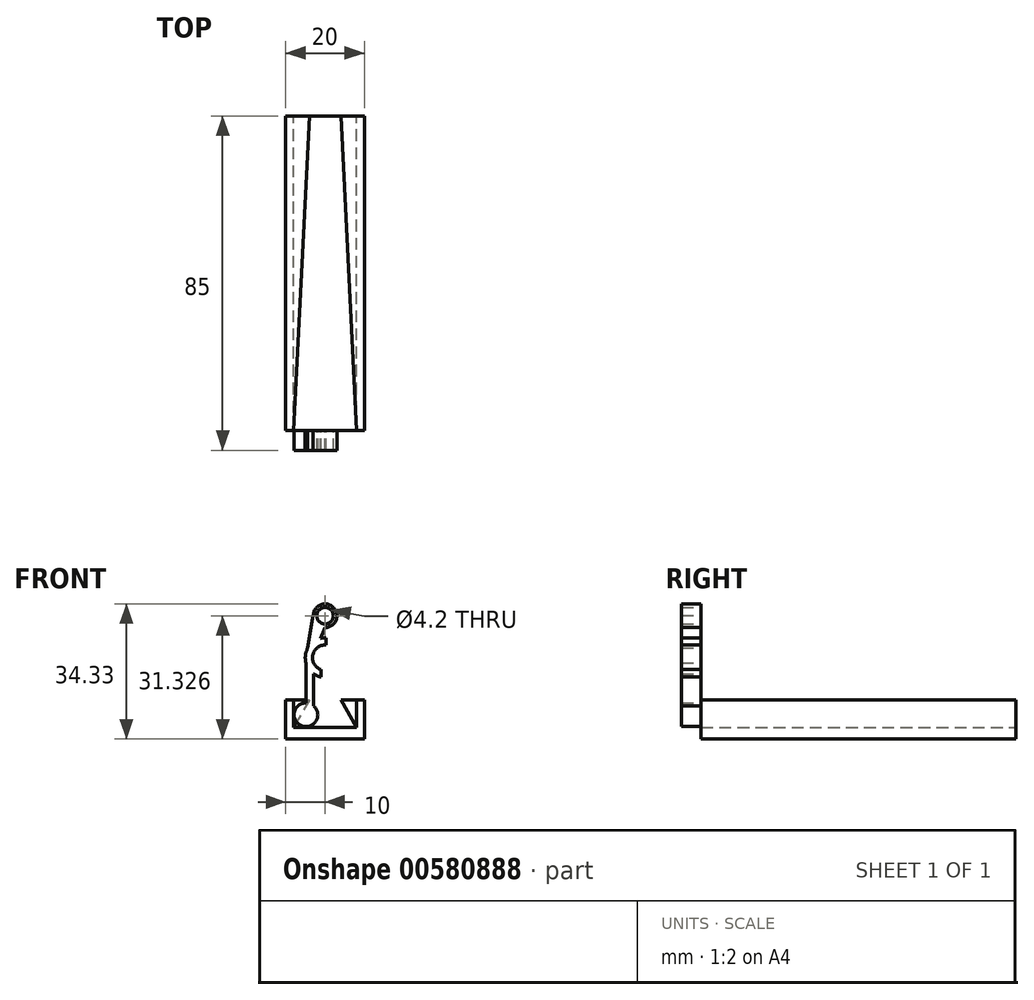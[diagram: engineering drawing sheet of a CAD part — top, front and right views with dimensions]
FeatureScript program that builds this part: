
annotation { "Feature Type Name" : "Feature", "Feature Type Description" : "" }
export const myFeature = defineFeature(function(context is Context, id is Id, definition is map)
    precondition{}
    {
        {
            var Q0;
            Q0=qCreatedBy(makeId("Front.planeOp"),FACE);
            var sketch = newSketch(context, id + "F0", { "sketchPlane" : qUnion([Q0])});
            skLineSegment(sketch, "E0.bottom", {"start": v(-10, 0) * mm, "end": v(10, 0) * mm});
            skLineSegment(sketch, "E0.top", {"start": v(-10, 10) * mm, "end": v(10, 10) * mm});
            skLineSegment(sketch, "E0.left", {"start": v(-10, 0) * mm, "end": v(-10, 10) * mm});
            skLineSegment(sketch, "E0.right", {"start": v(10, 0) * mm, "end": v(10, 10) * mm});
            skSolve(sketch);
        }
        {
            var Q0;
            Q0=makeQuery(id+"F0.imprint","IMPRINT",FACE,{"disambiguationData":[TD([[makeQuery(id+"F0.imprint","IMPRINT",EDGE,{"derivedFrom":sQuery(id+"F0.wireOp",EDGE,"E0.bottom")}),1.0]])]});
            extrude(context, id + "F1", {"entities" : qUnion([Q0]), "oppositeDirection" : true, "depth" : 80 * mm, "offsetDistance" : 25 * mm});
        }
        {
            var Q0;
            Q0=makeQuery(id+"F1.opExtrude","CAP_FACE",FACE,{"disambiguationData":[OSD([sQuery(id+"F0.wireOp",EDGE,"E0.bottom"),sQuery(id+"F0.wireOp",EDGE,"E0.top"),sQuery(id+"F0.wireOp",EDGE,"E0.left"),sQuery(id+"F0.wireOp",EDGE,"E0.right")])],"isStart":true});
            var sketch = newSketch(context, id + "F2", { "sketchPlane" : qUnion([Q0])});
            skLineSegment(sketch, "E1", {"start": v(0, 0) * mm, "end": v(0, 12.76) * mm, "construction": true});
            skLineSegment(sketch, "E2", {"start": v(-8, 10) * mm, "end": v(8, 10) * mm});
            skLineSegment(sketch, "E3", {"start": v(-8, 10) * mm, "end": v(-8, 3) * mm});
            skLineSegment(sketch, "E4", {"start": v(-8, 3) * mm, "end": v(8, 3) * mm});
            skLineSegment(sketch, "E5", {"start": v(8, 10) * mm, "end": v(8, 3) * mm});
            skSolve(sketch);
        }
        {
            var Q0;
            Q0=makeQuery(id+"F1.opExtrude","CAP_FACE",FACE,{"disambiguationData":[OSD([sQuery(id+"F0.wireOp",EDGE,"E0.bottom"),sQuery(id+"F0.wireOp",EDGE,"E0.top"),sQuery(id+"F0.wireOp",EDGE,"E0.left"),sQuery(id+"F0.wireOp",EDGE,"E0.right")])],"isStart":false});
            var sketch = newSketch(context, id + "F3", { "sketchPlane" : qUnion([Q0])});
            skLineSegment(sketch, "E6", {"start": v(-4, 10) * mm, "end": v(4, 10) * mm});
            skLineSegment(sketch, "E7", {"start": v(4, 10) * mm, "end": v(8, 3) * mm});
            skLineSegment(sketch, "E8", {"start": v(8, 3) * mm, "end": v(-8, 3) * mm});
            skLineSegment(sketch, "E9", {"start": v(-8, 3) * mm, "end": v(-4, 10) * mm});
            skSolve(sketch);
        }
        {
            var Q1;
            Q1 = qSketchRegion(id + "F2", true);
            var Q2;
            Q2 = qSketchRegion(id + "F3", true);
            loft(context, id + "F4", {"operationType" : NewBodyOperationType.REMOVE, "sheetProfilesArray" : [{ "sheetProfileEntities" : qUnion([Q1]) }, { "sheetProfileEntities" : qUnion([Q2]) }]});
        }
        {
            var Q0;
            Q0=qCreatedBy(makeId("Front.planeOp"),FACE);
            var sketch = newSketch(context, id + "F5", { "sketchPlane" : qUnion([Q0])});
            skLineSegment(sketch, "E10", {"start": v(0, 0) * mm, "end": v(0, 38.74) * mm, "construction": true});
            skCircle(sketch, "E11", {"center": v(0, 31.33) * mm, "radius": 3 * mm});
            skCircle(sketch, "E12", {"center": v(-4.85, 6.17) * mm, "radius": 3.01 * mm});
            skLineSegment(sketch, "E13.bottom", {"start": v(-2.9, 19.35) * mm, "end": v(-4.85, 19.35) * mm});
            skLineSegment(sketch, "E13.top", {"start": v(-2.9, 6.17) * mm, "end": v(-4.85, 6.17) * mm});
            skLineSegment(sketch, "E13.left", {"start": v(-2.9, 19.35) * mm, "end": v(-2.9, 6.17) * mm});
            skLineSegment(sketch, "E13.right", {"start": v(-4.85, 19.35) * mm, "end": v(-4.85, 6.17) * mm});
            skCircle(sketch, "E14", {"center": v(0, 20.68) * mm, "radius": 3.2 * mm});
            skCircle(sketch, "E15", {"center": v(0, 20.68) * mm, "radius": 5.03 * mm});
            skLineSegment(sketch, "E16.bottom", {"start": v(-0.97, 17.63) * mm, "end": v(0.97, 17.63) * mm});
            skLineSegment(sketch, "E16.top", {"start": v(-0.97, 15.08) * mm, "end": v(0.97, 15.08) * mm});
            skLineSegment(sketch, "E16.left", {"start": v(-0.97, 17.63) * mm, "end": v(-0.97, 15.08) * mm});
            skLineSegment(sketch, "E16.right", {"start": v(0.97, 17.63) * mm, "end": v(0.97, 15.08) * mm});
            skLineSegment(sketch, "E17", {"start": v(-3, 31.39) * mm, "end": v(-4.42, 23.08) * mm});
            skLineSegment(sketch, "E18", {"start": v(0, 28.33) * mm, "end": v(-1.17, 25.57) * mm});
            skCircle(sketch, "E19", {"center": v(0, 31.33) * mm, "radius": 2.1 * mm});
            skLineSegment(sketch, "E20", {"start": v(0.19, 25.7) * mm, "end": v(0.19, 23.87) * mm});
            skSolve(sketch);
        }
        {
            var Q0;
            {var subQ5=sQuery(id+"F5.wireOp",EDGE,"E13.top");Q0=makeQuery(id+"F5.imprint","IMPRINT",FACE,{"disambiguationData":[TD([[makeQuery(id+"F5.imprint","IMPRINT",EDGE,{"derivedFrom":subQ5}),1.0]])]});}
            var Q1;
            {var subQ5=sQuery(id+"F5.wireOp",EDGE,"E13.top");Q1=makeQuery(id+"F5.imprint","IMPRINT",FACE,{"disambiguationData":[TD([[makeQuery(id+"F5.imprint","IMPRINT",EDGE,{"derivedFrom":subQ5}),-1.0]])]});}
            var Q2;
            {var subQ0=sQuery(id+"F5.wireOp",EDGE,"E13.left");var subQ1=sQuery(id+"F5.wireOp",EDGE,"E12");var subQ2=makeQuery(id+"F5.imprint","INTERSECT",VERTEX,{"derivedFrom":[subQ1,subQ0]});Q2=makeQuery(id+"F5.imprint","IMPRINT",FACE,{"disambiguationData":[TD([[makeQuery(id+"F5.imprint","IMPRINT",EDGE,{"disambiguationData":[TD([[subQ2,-1.0]])],"derivedFrom":subQ1}),-1.0]])]});}
            var Q3;
            {var subQ1=sQuery(id+"F5.wireOp",EDGE,"E13.left");var subQ3=sQuery(id+"F5.wireOp",EDGE,"E15");var subQ4=makeQuery(id+"F5.imprint","INTERSECT",VERTEX,{"derivedFrom":[subQ1,subQ3]});Q3=makeQuery(id+"F5.imprint","IMPRINT",FACE,{"disambiguationData":[TD([[makeQuery(id+"F5.imprint","IMPRINT",EDGE,{"disambiguationData":[TD([[subQ4,-1.0]])],"derivedFrom":subQ3}),1.0]])]});}
            var Q4;
            {var subQ0=sQuery(id+"F5.wireOp",EDGE,"E13.bottom");Q4=makeQuery(id+"F5.imprint","IMPRINT",FACE,{"disambiguationData":[TD([[makeQuery(id+"F5.imprint","IMPRINT",EDGE,{"derivedFrom":subQ0}),1.0]])]});}
            var Q5;
            {var subQ1=sQuery(id+"F5.wireOp",EDGE,"E13.bottom");Q5=makeQuery(id+"F5.imprint","IMPRINT",FACE,{"disambiguationData":[TD([[makeQuery(id+"F5.imprint","IMPRINT",EDGE,{"derivedFrom":subQ1}),-1.0]])]});}
            var Q6;
            {var subQ3=sQuery(id+"F5.wireOp",EDGE,"E18");Q6=makeQuery(id+"F5.imprint","IMPRINT",FACE,{"disambiguationData":[TD([[makeQuery(id+"F5.imprint","IMPRINT",EDGE,{"derivedFrom":subQ3}),-1.0]])]});}
            var Q7;
            {var subQ0=sQuery(id+"F5.wireOp",EDGE,"E11");var subQ1=makeQuery(id+"F5.imprint","INTERSECT",VERTEX,{"derivedFrom":[subQ0,sQuery(id+"F5.wireOp",EDGE,"E17")]});Q7=makeQuery(id+"F5.imprint","IMPRINT",FACE,{"disambiguationData":[TD([[makeQuery(id+"F5.imprint","IMPRINT",EDGE,{"disambiguationData":[TD([[subQ1,-1.0]])],"derivedFrom":subQ0}),1.0]])]});}
            extrude(context, id + "F6", {"entities" : qUnion([Q0, Q1, Q2, Q3, Q4, Q5, Q6, Q7]), "depth" : 5 * mm, "offsetDistance" : 25 * mm});
        }
    });
